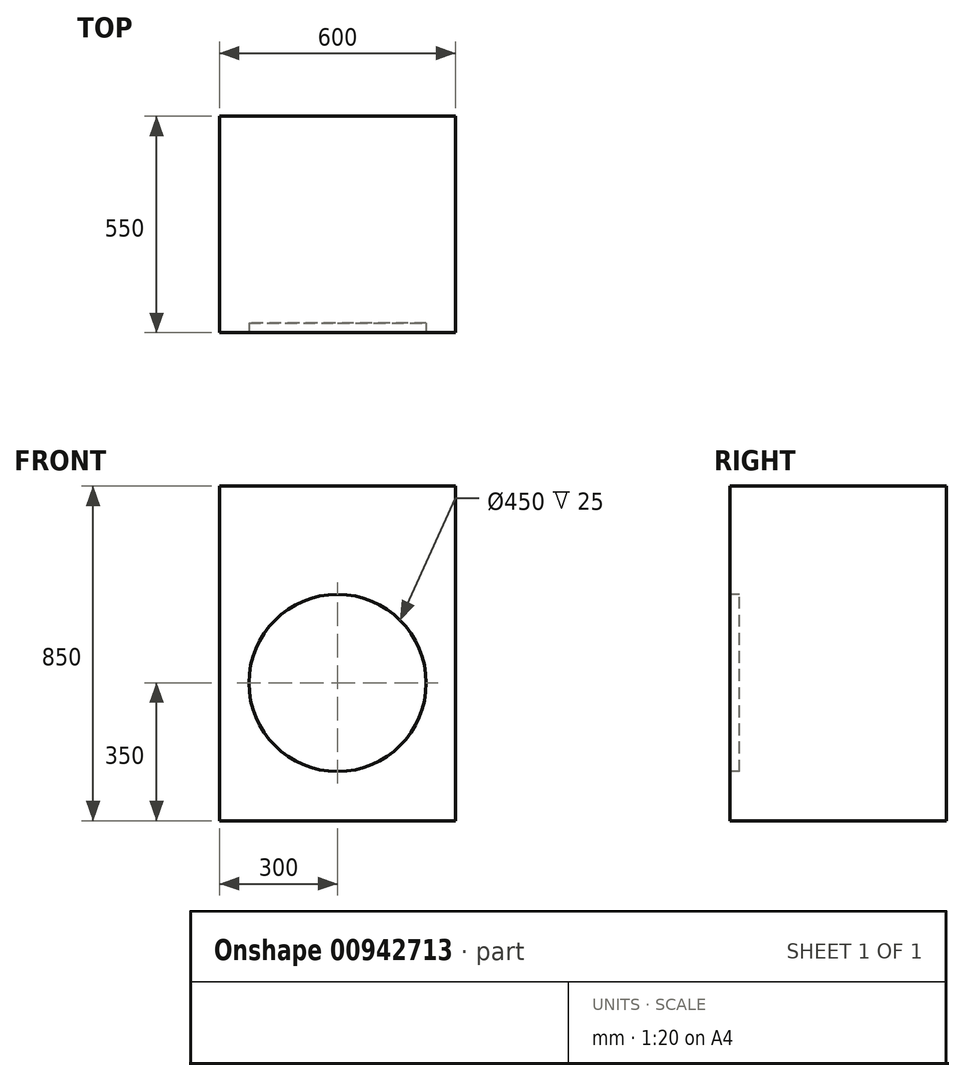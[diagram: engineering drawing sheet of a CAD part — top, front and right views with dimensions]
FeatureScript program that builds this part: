
annotation { "Feature Type Name" : "Feature", "Feature Type Description" : "" }
export const myFeature = defineFeature(function(context is Context, id is Id, definition is map)
    precondition{}
    {
        {
            var Q0;
            Q0=qCreatedBy(makeId("Top.planeOp"),FACE);
            var sketch = newSketch(context, id + "F0", { "sketchPlane" : qUnion([Q0])});
            skLineSegment(sketch, "E0.bottom", {"start": v(-300, -275) * mm, "end": v(300, -275) * mm});
            skLineSegment(sketch, "E0.top", {"start": v(-300, 275) * mm, "end": v(300, 275) * mm});
            skLineSegment(sketch, "E0.left", {"start": v(-300, -275) * mm, "end": v(-300, 275) * mm});
            skLineSegment(sketch, "E0.right", {"start": v(300, -275) * mm, "end": v(300, 275) * mm});
            skLineSegment(sketch, "E1", {"start": v(0, 275) * mm, "end": v(0, 0) * mm, "construction": true});
            skLineSegment(sketch, "E2", {"start": v(0, 0) * mm, "end": v(0, -275) * mm, "construction": true});
            skLineSegment(sketch, "E3", {"start": v(300, 0) * mm, "end": v(0, 0) * mm, "construction": true});
            skLineSegment(sketch, "E4", {"start": v(0, 0) * mm, "end": v(-300, 0) * mm, "construction": true});
            skSolve(sketch);
        }
        {
            var Q0;
            Q0 = qSketchRegion(id + "F0", true);
            extrude(context, id + "F1", {"entities" : qUnion([Q0]), "depth" : 850 * mm, "offsetDistance" : 25 * mm});
        }
        {
            var Q0;
            Q0=makeQuery(id+"F1.opExtrude","SWEPT_FACE",FACE,{"disambiguationData":[OSD([sQuery(id+"F0.wireOp",EDGE,"E0.bottom")])]});
            var sketch = newSketch(context, id + "F2", { "sketchPlane" : qUnion([Q0])});
            skCircle(sketch, "E5", {"center": v(0, 350) * mm, "radius": 225 * mm});
            skSolve(sketch);
        }
        {
            var Q0;
            Q0=makeQuery(id+"F2.imprint","IMPRINT",FACE,{"disambiguationData":[TD([[makeQuery(id+"F2.imprint","IMPRINT",EDGE,{"derivedFrom":sQuery(id+"F2.wireOp",EDGE,"E5")}),1.0]])]});
            extrude(context, id + "F3", {"entities" : qUnion([Q0]), "operationType" : NewBodyOperationType.REMOVE, "oppositeDirection" : true, "depth" : 25 * mm, "offsetDistance" : 25 * mm});
        }
    });
